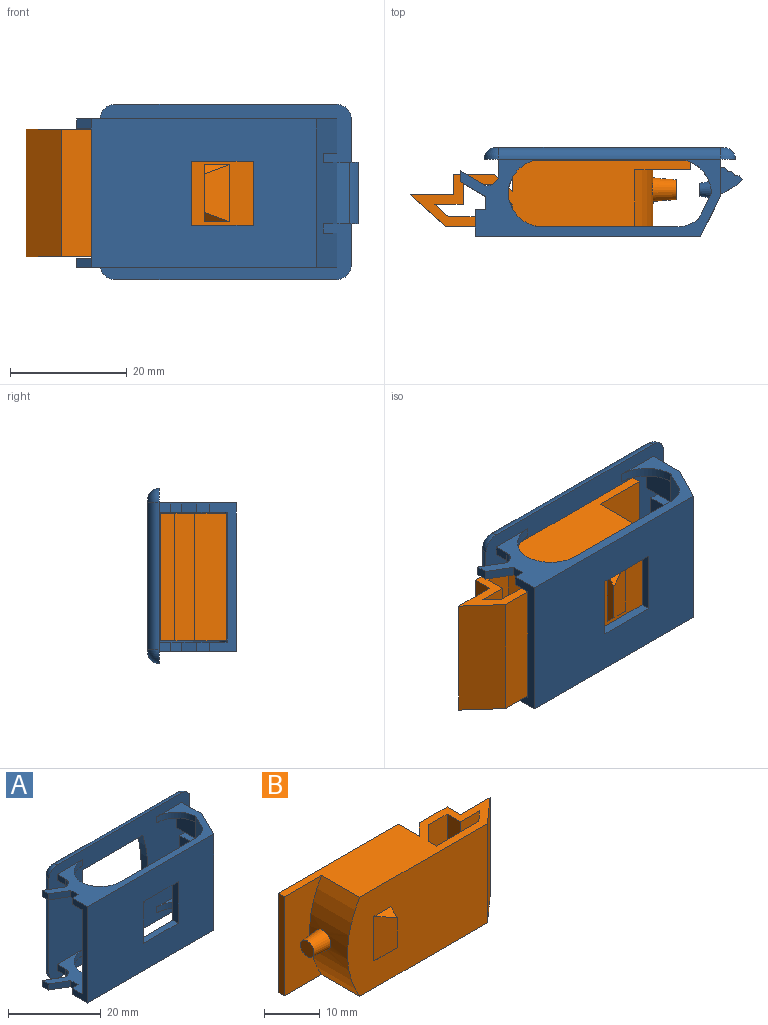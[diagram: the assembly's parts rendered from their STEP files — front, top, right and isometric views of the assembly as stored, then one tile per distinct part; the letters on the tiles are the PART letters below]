
ASSEMBLY  parts=2 mates=1
PART A: 80 faces, bbox 48.1x15.2x30 mm
  f0: plane 25.4x22.8mm, normal (0,1,0), area 462.5mm2, adj f10,f19,f20,f30,f76,f77,f78,f79
  f1: plane 38.5x25.4mm, normal (0,-1,0), area 861.3mm2, adj f11,f19,f20,f39,f76,f77,f78,f79
  f2: plane 3.89x0mm, normal (0,1,0), area 0mm2, adj f4,f7,f8,f75
  f3: plane 3.89x0mm, normal (0,1,0), area 0mm2, adj f4,f6,f8,f75
  f4: plane 10.5x4.83mm, normal (-1,0,0), area 45.3mm2, adj f2,f3,f5,f6,f7,f75
  f5: plane 10.5x1.6mm, normal (0,1,0), area 16.8mm2, adj f4,f6,f7,f65
  f6: plane 9.8x8.22mm, normal (0,0,1), area 26.3mm2, adj f3,f4,f5,f8,f10,f11,f12,f64
  f7: plane 9.8x8.22mm, normal (0,0,-1), area 26.3mm2, adj f2,f4,f5,f8,f10,f11,f12,f61
  f8: plane 10.5x4.45mm, normal (-0.89,0.45,0), area 50.5mm2, adj f2,f3,f6,f7,f10,f75
  f9: plane 5.85x4.45mm, normal (-0.89,0.45,0), area 29.1mm2, adj f10,f14,f19,f41,f63
  f10: cylinder r=6mm len=25.4mm, axis (0,0,-1), area 100.6mm2, adj f0,f6,f7,f8,f9,f19,f20,f29
  f11: plane 25.4x7mm, normal (0.89,-0.45,0), area 182.3mm2, adj f1,f6,f7,f12,f13,f19,f20,f40
  f12: plane 10.5x0.2mm, normal (1,0,0), area 2.1mm2, adj f6,f7,f11,f72
  f13: plane 6.2x5.85mm, normal (1,0,0), area 36.3mm2, adj f11,f17,f19,f63
  f14: plane 4.25x0mm, normal (0,1,0), area 0mm2, adj f9,f15,f59,f63
  f15: plane 5.83x4.25mm, normal (-1,0,0), area 24.8mm2, adj f14,f17,f59,f63
  f16: cylinder r=6mm len=6mm, axis (0,0,-1), area 14.8mm2, adj f17,f20,f29,f57
  f17: plane 43x30mm, normal (0,-1,0), area 843.4mm2, adj f13,f15,f16,f19,f20,f22,f23,f31
  f18: plane 39x26mm, normal (0,1,0), area 634.8mm2, adj f45,f46,f47,f48,f49,f50,f51,f52
  f19: plane 44.5x13.2mm, normal (0,0,1), area 154.4mm2, adj f0,f1,f9,f10,f11,f13,f17,f22
  f20: plane 44.5x13.2mm, normal (0,0,-1), area 154.4mm2, adj f0,f1,f10,f11,f16,f17,f21,f29
  f21: plane 1.86x1.6mm, normal (-1,0,0), area 3mm2, adj f20,f34,f36,f42
  f22: cylinder r=6mm len=6mm, axis (0,0,-1), area 15.1mm2, adj f17,f19,f30,f44
  f23: plane 2.54x1.6mm, normal (-1,0,0), area 4.1mm2, adj f17,f19,f24,f44
  f24: cylinder r=2mm len=2.2mm, axis (0,0,-1), area 5.4mm2, adj f19,f23,f25,f44
  f25: plane 4.3x2.54mm, normal (0.51,0.86,0), area 8mm2, adj f19,f24,f35,f44
  f26: plane 4.3x2.54mm, normal (-0.51,-0.86,0), area 8mm2, adj f19,f27,f35,f44
  f27: plane 2.2x1.6mm, normal (-1,0,0), area 3.5mm2, adj f19,f26,f28,f44
  f28: plane 1.8x1.6mm, normal (0,1,0), area 2.9mm2, adj f19,f27,f39,f44
  f29: plane 5.85x4.45mm, normal (-0.89,0.45,0), area 29.1mm2, adj f10,f16,f20,f58,f62
  f30: cylinder r=6mm len=25.4mm, axis (0,0,-1), area 29.5mm2, adj f0,f19,f20,f22,f31,f42,f43,f44
  f31: cylinder r=6mm len=6mm, axis (0,0,-1), area 15.1mm2, adj f17,f20,f30,f42
  f32: plane 2.54x1.6mm, normal (-1,0,0), area 4.1mm2, adj f17,f20,f33,f42
  f33: cylinder r=2mm len=2.2mm, axis (0,0,-1), area 5.4mm2, adj f20,f32,f34,f42
  f34: plane 4.3x2.54mm, normal (0.51,0.86,0), area 8mm2, adj f20,f21,f33,f42
  f35: plane 1.86x1.6mm, normal (-1,0,0), area 3mm2, adj f19,f25,f26,f44
  f36: plane 4.3x2.54mm, normal (-0.51,-0.86,0), area 8mm2, adj f20,f21,f37,f42
  f37: plane 2.2x1.6mm, normal (-1,0,0), area 3.5mm2, adj f20,f36,f38,f42
  f38: plane 1.8x1.6mm, normal (0,1,0), area 2.9mm2, adj f20,f37,f39,f42
  f39: plane 25.4x4.6mm, normal (-1,0,0), area 50.2mm2, adj f1,f19,f20,f28,f38,f42,f43,f44
  f40: plane 6.2x5.85mm, normal (1,0,0), area 36.3mm2, adj f11,f17,f20,f62
  f41: cylinder r=6mm len=6mm, axis (0,0,-1), area 14.8mm2, adj f9,f17,f19,f59
  f42: plane 14.1x11.6mm, normal (0,0,1), area 63.7mm2, adj f17,f21,f30,f31,f32,f33,f34,f36
  f43: plane 22.2x11.57mm, normal (0,1,0), area 256.9mm2, adj f30,f39,f42,f44
  f44: plane 14.1x11.6mm, normal (0,0,-1), area 63.7mm2, adj f17,f22,f23,f24,f25,f26,f27,f28
  f45: cylinder r=2mm len=38mm, axis (1,0,0), area 119.4mm2, adj f17,f18,f46,f47
  f46: torus R=0.5mm, axis (0,-1,0), area 8.8mm2, adj f17,f18,f45,f48
  f47: torus R=0.5mm, axis (0,-1,0), area 8.8mm2, adj f17,f18,f45,f49
  f48: cylinder r=2mm len=25mm, axis (0,0,1), area 78.5mm2, adj f17,f18,f46,f50
  f49: cylinder r=2mm len=25mm, axis (0,0,-1), area 78.5mm2, adj f17,f18,f47,f51
  f50: torus R=0.5mm, axis (0,-1,0), area 8.8mm2, adj f17,f18,f48,f52
  f51: torus R=0.5mm, axis (0,-1,0), area 8.8mm2, adj f17,f18,f49,f52
  f52: cylinder r=2mm len=38mm, axis (-1,0,0), area 119.4mm2, adj f17,f18,f50,f51
  f53: plane 19.5x2mm, normal (1,0,0), area 39mm2, adj f17,f18,f54,f56
  f54: plane 18.4x2mm, normal (0,0,-1), area 36.8mm2, adj f17,f18,f53,f55
  f55: cylinder r=31.58mm len=19.5mm, axis (0,1,0), area 39.6mm2, adj f17,f18,f54,f56
  f56: plane 18.4x2mm, normal (0,0,1), area 36.8mm2, adj f17,f18,f53,f55
  f57: plane 6x5.83mm, normal (0,0,1), area 7.7mm2, adj f16,f17,f58,f60
  f58: plane 4.25x0mm, normal (0,1,0), area 0mm2, adj f29,f57,f60,f62
  f59: plane 6x5.83mm, normal (0,0,-1), area 7.7mm2, adj f14,f15,f17,f41
  f60: plane 5.83x4.25mm, normal (-1,0,0), area 24.8mm2, adj f17,f57,f58,f62
  f61: plane 2.29x1.6mm, normal (0,1,0), area 3.7mm2, adj f7,f10,f11,f62
  f62: plane 10.8x4.59mm, normal (0,0,1), area 18.3mm2, adj f10,f11,f17,f29,f40,f58,f60,f61
  f63: plane 10.8x4.59mm, normal (0,0,-1), area 18.3mm2, adj f9,f10,f11,f13,f14,f15,f17,f64
  f64: plane 2.29x1.6mm, normal (0,1,0), area 3.7mm2, adj f6,f10,f11,f63
  f65: plane 10.5x0.4mm, normal (1,0,0), area 4.2mm2, adj f5,f6,f7,f66
  f66: plane 10.5x0.69mm, normal (0,1,0), area 7.3mm2, adj f6,f7,f65,f67
  f67: plane 10.5x0.7mm, normal (0.81,0.59,0), area 9.1mm2, adj f6,f7,f66,f68
  f68: plane 10.5x0.7mm, normal (0,1,0), area 7.3mm2, adj f6,f7,f67,f69
  f69: plane 10.5x0.7mm, normal (0.81,0.59,0), area 9.1mm2, adj f6,f7,f68,f70
  f70: plane 10.5x0.7mm, normal (0,1,0), area 7.3mm2, adj f6,f7,f69,f71
  f71: plane 10.5x0.7mm, normal (0.81,0.59,0), area 9.1mm2, adj f6,f7,f70,f73
  f72: plane 10.5x2.21mm, normal (0.5,-0.87,0), area 26.8mm2, adj f6,f7,f12,f73
  f73: cylinder r=5mm len=10.5mm, axis (0,0,1), area 19.8mm2, adj f6,f7,f71,f72
  f74: plane 2.2x2.2mm, normal (-1,0,0), area 3.8mm2, adj f75
  f75: cone r=1.1mm half-angle=11.3deg, axis (1,0,0), area 15.8mm2, adj f2,f3,f4,f8,f74
  f76: plane 11x1.6mm, normal (-1,0,0), area 17.6mm2, adj f0,f1,f77,f79
  f77: plane 10.6x1.6mm, normal (0,0,-1), area 17mm2, adj f0,f1,f76,f78
  f78: plane 11x1.6mm, normal (1,0,0), area 17.6mm2, adj f0,f1,f77,f79
  f79: plane 10.6x1.6mm, normal (0,0,1), area 17mm2, adj f0,f1,f76,f78
PART B: 35 faces, bbox 48x12.9x21.8 mm
  f0: plane 9.8x1.6mm, normal (1,0,0), area 13.1mm2, adj f1,f3,f33,f34
  f1: plane 9.8x4.3mm, normal (-0.35,-0.94,0), area 37.6mm2, adj f0,f3,f33,f34
  f2: plane 48x11.28mm, normal (0,0,-1), area 311.2mm2, adj f3,f4,f6,f7,f8,f9,f10,f11
  f3: plane 35.56x21.8mm, normal (0,-1,0), area 711.2mm2, adj f0,f1,f2,f5,f14,f21,f33,f34
  f4: plane 30.5x21.8mm, normal (0,1,0), area 278.6mm2, adj f2,f5,f12,f19,f22,f23,f25,f26
  f5: plane 48x11.28mm, normal (0,0,1), area 311.2mm2, adj f3,f4,f6,f7,f8,f9,f10,f11
  f6: plane 21.8x2.05mm, normal (1,0,0), area 44.6mm2, adj f2,f5,f7,f20
  f7: plane 21.8x3.65mm, normal (0.7,-0.72,0), area 111mm2, adj f2,f5,f6,f8
  f8: plane 21.8x4.75mm, normal (0,-1,0), area 103.5mm2, adj f2,f5,f7,f9
  f9: plane 21.8x3.4mm, normal (-1,0,0), area 74.1mm2, adj f2,f5,f8,f10
  f10: plane 21.8x4.91mm, normal (0,-1,0), area 107mm2, adj f2,f5,f9,f11
  f11: plane 21.8x2.46mm, normal (-0.67,0.75,0), area 72mm2, adj f2,f5,f10,f20
  f12: plane 21.8x1.6mm, normal (-1,0,0), area 34.9mm2, adj f2,f4,f5,f13
  f13: plane 21.8x9.5mm, normal (0,-1,0), area 161.3mm2, adj f2,f5,f12,f21
  f14: plane 21.8x6.04mm, normal (0.67,-0.75,0), area 176.7mm2, adj f2,f3,f5,f15
  f15: plane 21.8x7.5mm, normal (0,1,0), area 163.5mm2, adj f2,f5,f14,f16
  f16: plane 21.8x3.4mm, normal (1,0,0), area 74.1mm2, adj f2,f5,f15,f17
  f17: plane 21.8x7mm, normal (0,1,0), area 152.6mm2, adj f2,f5,f16,f18
  f18: plane 21.8x3mm, normal (-0.7,0.72,0), area 91.3mm2, adj f2,f5,f17,f19
  f19: plane 21.8x5.4mm, normal (1,0,0), area 117.7mm2, adj f2,f4,f5,f18
  f20: plane 21.8x10.84mm, normal (0,1,0), area 236.4mm2, adj f2,f5,f6,f11
  f21: cylinder r=20.71mm len=21.8mm, axis (0,-1,0), area 209.3mm2, adj f2,f3,f5,f13,f32
  f22: plane 18.48x9.68mm, normal (0,0,1), area 178.9mm2, adj f4,f24,f25,f26
  f23: plane 18.48x9.68mm, normal (0,0,-1), area 178.9mm2, adj f4,f24,f25,f26
  f24: plane 20.9x18.6mm, normal (0,1,0), area 374.2mm2, adj f22,f23,f25,f26
  f25: plane 18.6x9.68mm, normal (-1,0,0), area 180mm2, adj f4,f22,f23,f24
  f26: cylinder r=19.11mm len=18.6mm, axis (0,-1,0), area 188mm2, adj f4,f22,f23,f24
  f27: plane 4.6x3.98mm, normal (0,1,0), area 9.2mm2, adj f28,f29,f30
  f28: cylinder r=0.2mm len=4.68mm, axis (0.87,0,-0.5), area 1.5mm2, adj f4,f27,f29,f30
  f29: cylinder r=0.2mm len=5.29mm, axis (0,0,1), area 1.5mm2, adj f4,f27,f28,f30
  f30: cylinder r=0.2mm len=4.68mm, axis (-0.87,0,-0.5), area 1.5mm2, adj f4,f27,f28,f29
  f31: plane 3.4x3.4mm, normal (-1,0,0), area 9.1mm2, adj f32
  f32: cone r=1.7mm half-angle=4.6deg, axis (1,0,0), area 47.5mm2, adj f21,f31
  f33: plane 4.3x1.6mm, normal (0,-0.71,0.71), area 4.9mm2, adj f0,f1,f3
  f34: plane 4.3x1.6mm, normal (0,-0.71,-0.71), area 4.9mm2, adj f0,f1,f3
PLACE A t=(14.86,13.57,3.15)mm
PLACE B rot(axis=(0,1,0),180deg) t=(6.66,13.33,26.75)mm
MATE slider B.f32 <-> A.f75  axis (1,0,0) through (28.26,13.97,15.85)mm
